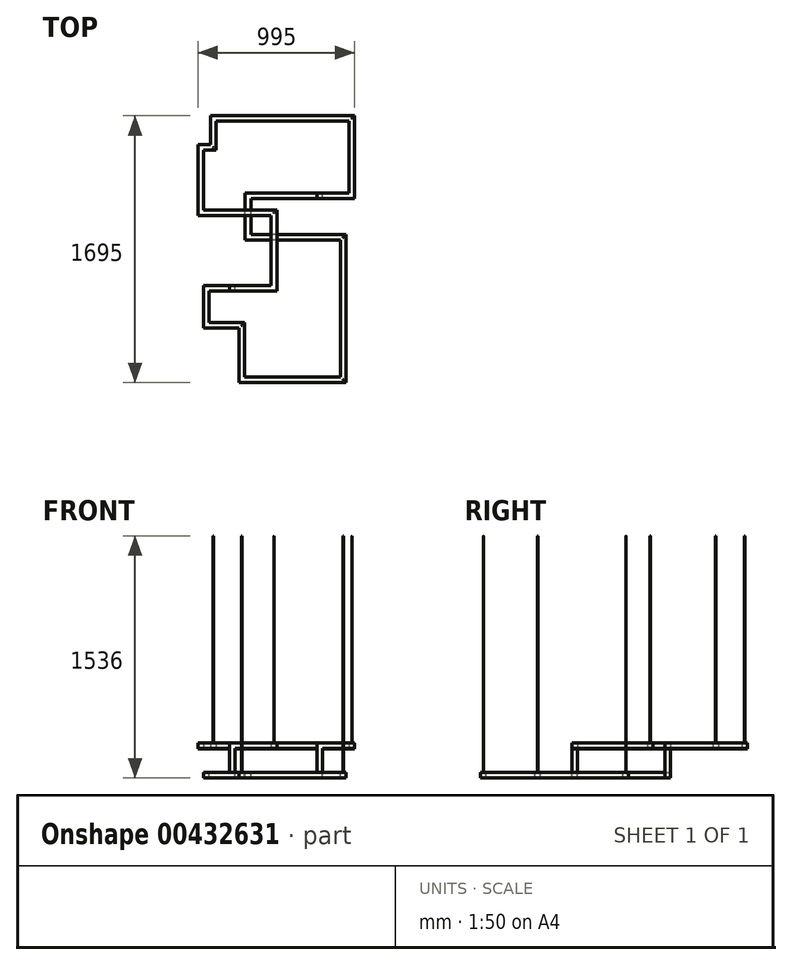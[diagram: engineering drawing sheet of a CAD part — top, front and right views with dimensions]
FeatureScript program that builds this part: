
annotation { "Feature Type Name" : "Feature", "Feature Type Description" : "" }
export const myFeature = defineFeature(function(context is Context, id is Id, definition is map)
    precondition{}
    {
        {
            var Q0;
            Q0=qCreatedBy(makeId("Top.planeOp"),FACE);
            var sketch = newSketch(context, id + "F0", { "sketchPlane" : qUnion([Q0])});
            skLineSegment(sketch, "E0", {"start": v(519.01, 860.28) * mm, "end": v(-510.57, -839.72) * mm, "construction": true});
            skLineSegment(sketch, "E1", {"start": v(-510.57, 860.28) * mm, "end": v(519.01, -839.72) * mm, "construction": true});
            skLineSegment(sketch, "E2", {"start": v(-313.44, -240) * mm, "end": v(-17.5, -240) * mm, "construction": true});
            skLineSegment(sketch, "E3", {"start": v(-17.5, -240) * mm, "end": v(-17.5, 240) * mm, "construction": true});
            skLineSegment(sketch, "E4", {"start": v(-17.5, 240) * mm, "end": v(-482.5, 240) * mm, "construction": true});
            skLineSegment(sketch, "E5", {"start": v(-482.5, 240) * mm, "end": v(-482.5, 655) * mm, "construction": true});
            skLineSegment(sketch, "E6", {"start": v(-482.5, 655) * mm, "end": v(-402.5, 655) * mm, "construction": true});
            skLineSegment(sketch, "E7", {"start": v(-402.5, 655) * mm, "end": v(-402.5, 840) * mm, "construction": true});
            skLineSegment(sketch, "E8", {"start": v(-402.5, 840) * mm, "end": v(477.5, 840) * mm, "construction": true});
            skLineSegment(sketch, "E9", {"start": v(477.5, 840) * mm, "end": v(477.5, 350) * mm, "construction": true});
            skLineSegment(sketch, "E10", {"start": v(477.5, 350) * mm, "end": v(294.36, 350) * mm, "construction": true});
            skLineSegment(sketch, "E11.0", {"start": v(460, 367.5) * mm, "end": v(255, 367.5) * mm});
            skLineSegment(sketch, "E11.1", {"start": v(460, 822.5) * mm, "end": v(460, 367.5) * mm});
            skLineSegment(sketch, "E11.2", {"start": v(-385, 822.5) * mm, "end": v(460, 822.5) * mm});
            skLineSegment(sketch, "E11.3", {"start": v(-385, 637.5) * mm, "end": v(-385, 822.5) * mm});
            skLineSegment(sketch, "E11.4", {"start": v(-465, 637.5) * mm, "end": v(-385, 637.5) * mm});
            skLineSegment(sketch, "E11.5", {"start": v(-300, -257.5) * mm, "end": v(0, -257.5) * mm});
            skLineSegment(sketch, "E11.6", {"start": v(0, -257.5) * mm, "end": v(0, 257.5) * mm});
            skLineSegment(sketch, "E11.7", {"start": v(0, 257.5) * mm, "end": v(-465, 257.5) * mm});
            skLineSegment(sketch, "E11.8", {"start": v(-465, 257.5) * mm, "end": v(-465, 637.5) * mm});
            skLineSegment(sketch, "E12.0", {"start": v(495, 332.5) * mm, "end": v(255, 332.5) * mm});
            skLineSegment(sketch, "E12.1", {"start": v(495, 857.5) * mm, "end": v(495, 332.5) * mm});
            skLineSegment(sketch, "E12.2", {"start": v(-420, 857.5) * mm, "end": v(495, 857.5) * mm});
            skLineSegment(sketch, "E12.3", {"start": v(-420, 672.5) * mm, "end": v(-420, 857.5) * mm});
            skLineSegment(sketch, "E12.4", {"start": v(-500, 672.5) * mm, "end": v(-420, 672.5) * mm});
            skLineSegment(sketch, "E12.5", {"start": v(-300, -222.5) * mm, "end": v(-35, -222.5) * mm});
            skLineSegment(sketch, "E12.6", {"start": v(-35, -222.5) * mm, "end": v(-35, 222.5) * mm});
            skLineSegment(sketch, "E12.7", {"start": v(-35, 222.5) * mm, "end": v(-500, 222.5) * mm});
            skLineSegment(sketch, "E12.8", {"start": v(-500, 222.5) * mm, "end": v(-500, 672.5) * mm});
            skLineSegment(sketch, "E13", {"start": v(255, 367.5) * mm, "end": v(255, 332.5) * mm});
            skLineSegment(sketch, "E14", {"start": v(-300, -257.5) * mm, "end": v(-300, -222.5) * mm});
            skSolve(sketch);
        }
        {
            var Q0;
            Q0 = qSketchRegion(id + "F0", true);
            extrude(context, id + "F1", {"entities" : qUnion([Q0]), "depth" : 35 * mm});
        }
        {
            var Q0;
            Q0=qCreatedBy(makeId("Top.planeOp"),FACE);
            var sketch = newSketch(context, id + "F2", { "sketchPlane" : qUnion([Q0])});
            skLineSegment(sketch, "E15.bottom", {"start": v(-300, -257.5) * mm, "end": v(-265, -257.5) * mm});
            skLineSegment(sketch, "E15.top", {"start": v(-300, -222.5) * mm, "end": v(-265, -222.5) * mm});
            skLineSegment(sketch, "E15.left", {"start": v(-300, -257.5) * mm, "end": v(-300, -222.5) * mm});
            skLineSegment(sketch, "E15.right", {"start": v(-265, -257.5) * mm, "end": v(-265, -222.5) * mm});
            skLineSegment(sketch, "E16.bottom", {"start": v(255, 332.5) * mm, "end": v(290, 332.5) * mm});
            skLineSegment(sketch, "E16.top", {"start": v(255, 367.5) * mm, "end": v(290, 367.5) * mm});
            skLineSegment(sketch, "E16.left", {"start": v(255, 332.5) * mm, "end": v(255, 367.5) * mm});
            skLineSegment(sketch, "E16.right", {"start": v(290, 332.5) * mm, "end": v(290, 367.5) * mm});
            skSolve(sketch);
        }
        {
            var Q0;
            Q0 = qSketchRegion(id + "F2", true);
            extrude(context, id + "F3", {"entities" : qUnion([Q0]), "operationType" : NewBodyOperationType.ADD, "oppositeDirection" : true, "depth" : 150 * mm});
        }
        {
            var Q0;
            Q0=makeQuery(id+"F3.opExtrude","CAP_FACE",FACE,{"disambiguationData":[OSD([sQuery(id+"F2.wireOp",EDGE,"E15.bottom"),sQuery(id+"F2.wireOp",EDGE,"E15.top"),sQuery(id+"F2.wireOp",EDGE,"E15.left"),sQuery(id+"F2.wireOp",EDGE,"E15.right")])],"isStart":false});
            cPlane(context, id + "F4", {"entities" : qUnion([Q0]), "cplaneType" : CPlaneType.OFFSET, "offset" : 0 * mm, "width" : 150 * mm, "height" : 150 * mm});
        }
        {
            var Q0;
            Q0=qCreatedBy(id+"F4.planeOp",FACE);
            var sketch = newSketch(context, id + "F5", { "sketchPlane" : qUnion([Q0])});
            skLineSegment(sketch, "E17", {"start": v(-282.5, 240) * mm, "end": v(-447.5, 240) * mm, "construction": true});
            skLineSegment(sketch, "E18", {"start": v(-447.5, 240) * mm, "end": v(-447.5, 475) * mm, "construction": true});
            skLineSegment(sketch, "E19", {"start": v(-447.5, 475) * mm, "end": v(-222.5, 475) * mm, "construction": true});
            skLineSegment(sketch, "E20", {"start": v(-222.5, 475) * mm, "end": v(-222.5, 820) * mm, "construction": true});
            skLineSegment(sketch, "E21", {"start": v(-222.5, 820) * mm, "end": v(422.5, 820) * mm, "construction": true});
            skLineSegment(sketch, "E22", {"start": v(422.5, 820) * mm, "end": v(422.5, -85) * mm, "construction": true});
            skLineSegment(sketch, "E23", {"start": v(422.5, -85) * mm, "end": v(-182.5, -85) * mm, "construction": true});
            skLineSegment(sketch, "E24", {"start": v(-182.5, -85) * mm, "end": v(-182.5, -350) * mm, "construction": true});
            skLineSegment(sketch, "E25", {"start": v(-182.5, -350) * mm, "end": v(272.5, -350) * mm, "construction": true});
            skLineSegment(sketch, "E26.0", {"start": v(-200, -367.5) * mm, "end": v(290, -367.5) * mm});
            skLineSegment(sketch, "E26.1", {"start": v(-200, -67.5) * mm, "end": v(-200, -367.5) * mm});
            skLineSegment(sketch, "E26.2", {"start": v(405, -67.5) * mm, "end": v(-200, -67.5) * mm});
            skLineSegment(sketch, "E26.3", {"start": v(405, 802.5) * mm, "end": v(405, -67.5) * mm});
            skLineSegment(sketch, "E26.4", {"start": v(-205, 802.5) * mm, "end": v(405, 802.5) * mm});
            skLineSegment(sketch, "E26.5", {"start": v(-265, 257.5) * mm, "end": v(-430, 257.5) * mm});
            skLineSegment(sketch, "E26.6", {"start": v(-430, 257.5) * mm, "end": v(-430, 457.5) * mm});
            skLineSegment(sketch, "E26.7", {"start": v(-430, 457.5) * mm, "end": v(-205, 457.5) * mm});
            skLineSegment(sketch, "E26.8", {"start": v(-205, 457.5) * mm, "end": v(-205, 802.5) * mm});
            skLineSegment(sketch, "E27.0", {"start": v(-165, -332.5) * mm, "end": v(290, -332.5) * mm});
            skLineSegment(sketch, "E27.1", {"start": v(-165, -102.5) * mm, "end": v(-165, -332.5) * mm});
            skLineSegment(sketch, "E27.2", {"start": v(440, -102.5) * mm, "end": v(-165, -102.5) * mm});
            skLineSegment(sketch, "E27.3", {"start": v(440, 837.5) * mm, "end": v(440, -102.5) * mm});
            skLineSegment(sketch, "E27.4", {"start": v(-240, 837.5) * mm, "end": v(440, 837.5) * mm});
            skLineSegment(sketch, "E27.5", {"start": v(-265, 222.5) * mm, "end": v(-465, 222.5) * mm});
            skLineSegment(sketch, "E27.6", {"start": v(-465, 222.5) * mm, "end": v(-465, 492.5) * mm});
            skLineSegment(sketch, "E27.7", {"start": v(-465, 492.5) * mm, "end": v(-240, 492.5) * mm});
            skLineSegment(sketch, "E27.8", {"start": v(-240, 492.5) * mm, "end": v(-240, 837.5) * mm});
            skLineSegment(sketch, "E28", {"start": v(290, -367.5) * mm, "end": v(290, -332.5) * mm});
            skLineSegment(sketch, "E29", {"start": v(-265, 222.5) * mm, "end": v(-265, 257.5) * mm});
            skSolve(sketch);
        }
        {
            var Q0;
            Q0 = qSketchRegion(id + "F5", true);
            extrude(context, id + "F6", {"entities" : qUnion([Q0]), "operationType" : NewBodyOperationType.ADD, "depth" : 35 * mm});
        }
        {
            var Q0;
            Q0=makeQuery(id+"F6.opExtrude","CAP_FACE",FACE,{"disambiguationData":[OSD([sQuery(id+"F5.wireOp",EDGE,"E26.0"),sQuery(id+"F5.wireOp",EDGE,"E26.1"),sQuery(id+"F5.wireOp",EDGE,"E26.2"),sQuery(id+"F5.wireOp",EDGE,"E26.3"),sQuery(id+"F5.wireOp",EDGE,"E26.4"),sQuery(id+"F5.wireOp",EDGE,"E26.5"),sQuery(id+"F5.wireOp",EDGE,"E26.6"),sQuery(id+"F5.wireOp",EDGE,"E26.7"),sQuery(id+"F5.wireOp",EDGE,"E26.8"),sQuery(id+"F5.wireOp",EDGE,"E27.0"),sQuery(id+"F5.wireOp",EDGE,"E27.1"),sQuery(id+"F5.wireOp",EDGE,"E27.2"),sQuery(id+"F5.wireOp",EDGE,"E27.3"),sQuery(id+"F5.wireOp",EDGE,"E27.4"),sQuery(id+"F5.wireOp",EDGE,"E27.5"),sQuery(id+"F5.wireOp",EDGE,"E27.6"),sQuery(id+"F5.wireOp",EDGE,"E27.7"),sQuery(id+"F5.wireOp",EDGE,"E27.8"),sQuery(id+"F5.wireOp",EDGE,"E28"),sQuery(id+"F5.wireOp",EDGE,"E29")])],"isStart":false});
            extrude(context, id + "F7", {"entities" : qUnion([Q0]), "depth" : 1 * mm});
        }
        {
            var Q0;
            Q0=makeQuery(id+"F6.boolean.opBoolean","MERGE",FACE,{"derivedFrom":[makeQuery(id+"F3.opExtrude","SWEPT_FACE",FACE,{"disambiguationData":[OSD([sQuery(id+"F2.wireOp",EDGE,"E15.right")])]}),makeQuery(id+"F6.opExtrude","SWEPT_FACE",FACE,{"disambiguationData":[OSD([sQuery(id+"F5.wireOp",EDGE,"E29")])]})]});
            var Q1;
            Q1=makeQuery(id+"F6.boolean.opBoolean","MERGE",FACE,{"derivedFrom":[makeQuery(id+"F3.opExtrude","SWEPT_FACE",FACE,{"disambiguationData":[OSD([sQuery(id+"F2.wireOp",EDGE,"E16.right")])]}),makeQuery(id+"F6.opExtrude","SWEPT_FACE",FACE,{"disambiguationData":[OSD([sQuery(id+"F5.wireOp",EDGE,"E28")])]})]});
            extrude(context, id + "F8", {"entities" : qUnion([Q0, Q1]), "depth" : 1 * mm});
        }
        {
            var Q0;
            Q0=makeQuery(id+"F1.opExtrude","CAP_FACE",FACE,{"disambiguationData":[OSD([sQuery(id+"F0.wireOp",EDGE,"E11.0"),sQuery(id+"F0.wireOp",EDGE,"E11.1"),sQuery(id+"F0.wireOp",EDGE,"E11.2"),sQuery(id+"F0.wireOp",EDGE,"E11.3"),sQuery(id+"F0.wireOp",EDGE,"E11.4"),sQuery(id+"F0.wireOp",EDGE,"E11.5"),sQuery(id+"F0.wireOp",EDGE,"E11.6"),sQuery(id+"F0.wireOp",EDGE,"E11.7"),sQuery(id+"F0.wireOp",EDGE,"E11.8"),sQuery(id+"F0.wireOp",EDGE,"E12.0"),sQuery(id+"F0.wireOp",EDGE,"E12.1"),sQuery(id+"F0.wireOp",EDGE,"E12.2"),sQuery(id+"F0.wireOp",EDGE,"E12.3"),sQuery(id+"F0.wireOp",EDGE,"E12.4"),sQuery(id+"F0.wireOp",EDGE,"E12.5"),sQuery(id+"F0.wireOp",EDGE,"E12.6"),sQuery(id+"F0.wireOp",EDGE,"E12.7"),sQuery(id+"F0.wireOp",EDGE,"E12.8"),sQuery(id+"F0.wireOp",EDGE,"E13"),sQuery(id+"F0.wireOp",EDGE,"E14")])],"isStart":true});
            extrude(context, id + "F9", {"entities" : qUnion([Q0]), "depth" : 1 * mm});
        }
        {
            var Q0;
            Q0=makeQuery(id+"F6.opExtrude","CAP_FACE",FACE,{"disambiguationData":[OSD([sQuery(id+"F5.wireOp",EDGE,"E26.0"),sQuery(id+"F5.wireOp",EDGE,"E26.1"),sQuery(id+"F5.wireOp",EDGE,"E26.2"),sQuery(id+"F5.wireOp",EDGE,"E26.3"),sQuery(id+"F5.wireOp",EDGE,"E26.4"),sQuery(id+"F5.wireOp",EDGE,"E26.5"),sQuery(id+"F5.wireOp",EDGE,"E26.6"),sQuery(id+"F5.wireOp",EDGE,"E26.7"),sQuery(id+"F5.wireOp",EDGE,"E26.8"),sQuery(id+"F5.wireOp",EDGE,"E27.0"),sQuery(id+"F5.wireOp",EDGE,"E27.1"),sQuery(id+"F5.wireOp",EDGE,"E27.2"),sQuery(id+"F5.wireOp",EDGE,"E27.3"),sQuery(id+"F5.wireOp",EDGE,"E27.4"),sQuery(id+"F5.wireOp",EDGE,"E27.5"),sQuery(id+"F5.wireOp",EDGE,"E27.6"),sQuery(id+"F5.wireOp",EDGE,"E27.7"),sQuery(id+"F5.wireOp",EDGE,"E27.8"),sQuery(id+"F5.wireOp",EDGE,"E28"),sQuery(id+"F5.wireOp",EDGE,"E29")])],"isStart":true});
            var sketch = newSketch(context, id + "F10", { "sketchPlane" : qUnion([Q0])});
            skPoint(sketch, "E30", {"position": v(422.5, 85) * mm});
            skPoint(sketch, "E31", {"position": v(-222.5, -475) * mm});
            skCircle(sketch, "E32", {"center": v(-222.5, -475) * mm, "radius": 1 * mm});
            skCircle(sketch, "E33", {"center": v(422.5, 85) * mm, "radius": 1 * mm});
            skPoint(sketch, "E34", {"position": v(422.5, -820) * mm});
            skCircle(sketch, "E35", {"center": v(422.5, -820) * mm, "radius": 1 * mm});
            skSolve(sketch);
        }
        {
            var Q0;
            Q0 = qSketchRegion(id + "F10", true);
            extrude(context, id + "F11", {"entities" : qUnion([Q0]), "depth" : 1500 * mm});
        }
        {
            var Q0;
            Q0=makeQuery(id+"F1.opExtrude","CAP_FACE",FACE,{"disambiguationData":[OSD([sQuery(id+"F0.wireOp",EDGE,"E11.0"),sQuery(id+"F0.wireOp",EDGE,"E11.1"),sQuery(id+"F0.wireOp",EDGE,"E11.2"),sQuery(id+"F0.wireOp",EDGE,"E11.3"),sQuery(id+"F0.wireOp",EDGE,"E11.4"),sQuery(id+"F0.wireOp",EDGE,"E11.5"),sQuery(id+"F0.wireOp",EDGE,"E11.6"),sQuery(id+"F0.wireOp",EDGE,"E11.7"),sQuery(id+"F0.wireOp",EDGE,"E11.8"),sQuery(id+"F0.wireOp",EDGE,"E12.0"),sQuery(id+"F0.wireOp",EDGE,"E12.1"),sQuery(id+"F0.wireOp",EDGE,"E12.2"),sQuery(id+"F0.wireOp",EDGE,"E12.3"),sQuery(id+"F0.wireOp",EDGE,"E12.4"),sQuery(id+"F0.wireOp",EDGE,"E12.5"),sQuery(id+"F0.wireOp",EDGE,"E12.6"),sQuery(id+"F0.wireOp",EDGE,"E12.7"),sQuery(id+"F0.wireOp",EDGE,"E12.8"),sQuery(id+"F0.wireOp",EDGE,"E13"),sQuery(id+"F0.wireOp",EDGE,"E14")])],"isStart":false});
            var sketch = newSketch(context, id + "F12", { "sketchPlane" : qUnion([Q0])});
            skPoint(sketch, "E36", {"position": v(-17.5, 240) * mm});
            skPoint(sketch, "E37", {"position": v(-402.5, 655) * mm});
            skPoint(sketch, "E38", {"position": v(477.5, 840) * mm});
            skCircle(sketch, "E39", {"center": v(-402.5, 655) * mm, "radius": 1 * mm});
            skCircle(sketch, "E40", {"center": v(477.5, 840) * mm, "radius": 1 * mm});
            skCircle(sketch, "E41", {"center": v(-17.5, 240) * mm, "radius": 1 * mm});
            skSolve(sketch);
        }
        {
            var Q0;
            Q0 = qSketchRegion(id + "F12", true);
            extrude(context, id + "F13", {"entities" : qUnion([Q0]), "depth" : 1315 * mm});
        }
    });
